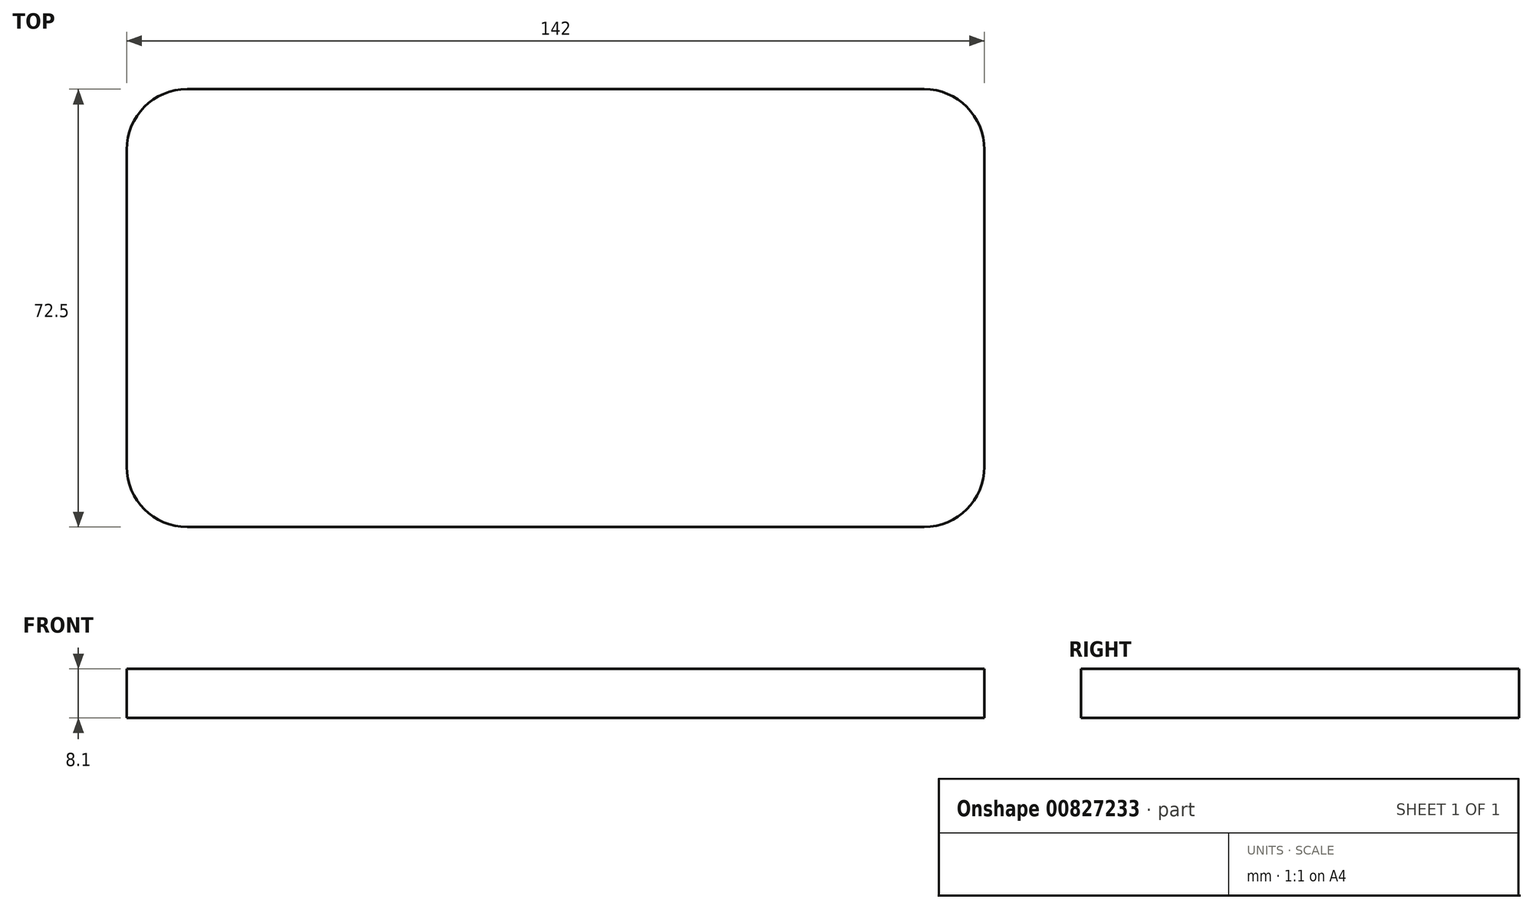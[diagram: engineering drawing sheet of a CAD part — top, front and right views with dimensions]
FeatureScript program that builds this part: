
annotation { "Feature Type Name" : "Feature", "Feature Type Description" : "" }
export const myFeature = defineFeature(function(context is Context, id is Id, definition is map)
    precondition{}
    {
        {
            var Q0;
            Q0=qCreatedBy(makeId("Top.planeOp"),FACE);
            var sketch = newSketch(context, id + "F0", { "sketchPlane" : qUnion([Q0])});
            skLineSegment(sketch, "E0.bottom", {"start": v(-56.9, 37.44) * mm, "end": v(65.1, 37.44) * mm});
            skLineSegment(sketch, "E0.top", {"start": v(-56.9, -35.06) * mm, "end": v(65.1, -35.06) * mm});
            skLineSegment(sketch, "E0.left", {"start": v(-66.9, 27.44) * mm, "end": v(-66.9, -25.06) * mm});
            skLineSegment(sketch, "E0.right", {"start": v(75.1, 27.44) * mm, "end": v(75.1, -25.06) * mm});
            skPoint(sketch, "E1.visualSharp", {"position": v(-66.9, 37.44) * mm});
            skArc(sketch, "E1.filletArc", {"start": v(-56.9, 37.44) * mm, "mid": v(-63.98, 34.5) * mm, "end": v(-66.9, 27.44) * mm});
            skPoint(sketch, "E2.visualSharp", {"position": v(75.1, 37.44) * mm});
            skArc(sketch, "E2.filletArc", {"start": v(75.1, 27.44) * mm, "mid": v(72.16, 34.5) * mm, "end": v(65.1, 37.44) * mm});
            skPoint(sketch, "E3.visualSharp", {"position": v(75.1, -35.06) * mm});
            skArc(sketch, "E3.filletArc", {"start": v(65.1, -35.06) * mm, "mid": v(72.16, -32.13) * mm, "end": v(75.1, -25.06) * mm});
            skPoint(sketch, "E4.visualSharp", {"position": v(-66.9, -35.06) * mm});
            skArc(sketch, "E4.filletArc", {"start": v(-66.9, -25.06) * mm, "mid": v(-63.98, -32.13) * mm, "end": v(-56.9, -35.06) * mm});
            skSolve(sketch);
        }
        {
            var Q0;
            Q0=makeQuery(id+"F0.imprint","IMPRINT",FACE,{"disambiguationData":[TD([[makeQuery(id+"F0.imprint","IMPRINT",EDGE,{"derivedFrom":sQuery(id+"F0.wireOp",EDGE,"E0.bottom")}),-1.0]])]});
            extrude(context, id + "F1", {"entities" : qUnion([Q0]), "depth" : 8.1 * mm, "offsetDistance" : 25 * mm});
        }
    });
